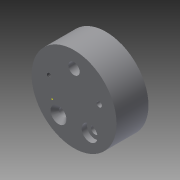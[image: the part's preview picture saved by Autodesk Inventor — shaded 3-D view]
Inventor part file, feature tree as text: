
AUTODESK INVENTOR PART (.ipt)
format: ipt  version: 2015 (Build 190159000, 159)  size: 105,472 bytes
history: native  units: in
note: dims shown in document units (in); Inventor stores cm internally (conversion verified against a paired STEP export)
features: hole x5, sketch x4, extrude x1
ambient origin geometry x8: Origin, YZ Plane, XZ Plane, XY Plane, X Axis, Y Axis, Z Axis, Center Point
bodies: Solid1 (feature_tree)
feature tree (10):
  extrude  "Extrusion1"  Depth=1.5in TaperAngle=0.0deg
  sketch  "Sketch2"  dims[d3=1.9685in d5=360.0deg]
  sketch  "Sketch3"  dims[d7=0.25in d8=0.75in d9=0.375in d10=0.25in d11=0.5635in d12=1.0in d13=0.8108in]
  sketch  "Sketch4"  dims[d14=0.375in d15=0.75in d16=0.75in d17=0.25in d18=0.5635in d19=1.0in d20=0.8108in d21=0.375in d22=0.75in d23=0.75in d24=0.25in d25=0.5635in d26=1.0in d27=0.8108in d28=0.196in d29=0.5in d30=0.75in d31=0.25in d32=0.5635in d33=0.75in d34=0.8108in d35=0.531in d36=0.5in d37=1.125in d38=0.364in d39=0.5635in d40=0.75in d41=0.8108in]
  hole  "Hole1"  [1 undecoded]
  hole  "Hole2"  [1 undecoded]
  hole  "Hole3"  [1 undecoded]
  hole  "Hole4"  [1 undecoded]
  hole  "Hole5"  [1 undecoded]
  sketch  "Sketch1"  dims[d0=4.0in d1=1.5in d2=0.0in]
note: 5 required parameter values undecoded (feature->parameter linkage not recoverable at this tier; creation-order binding heuristic only, values carry confidence <= 0.55)
